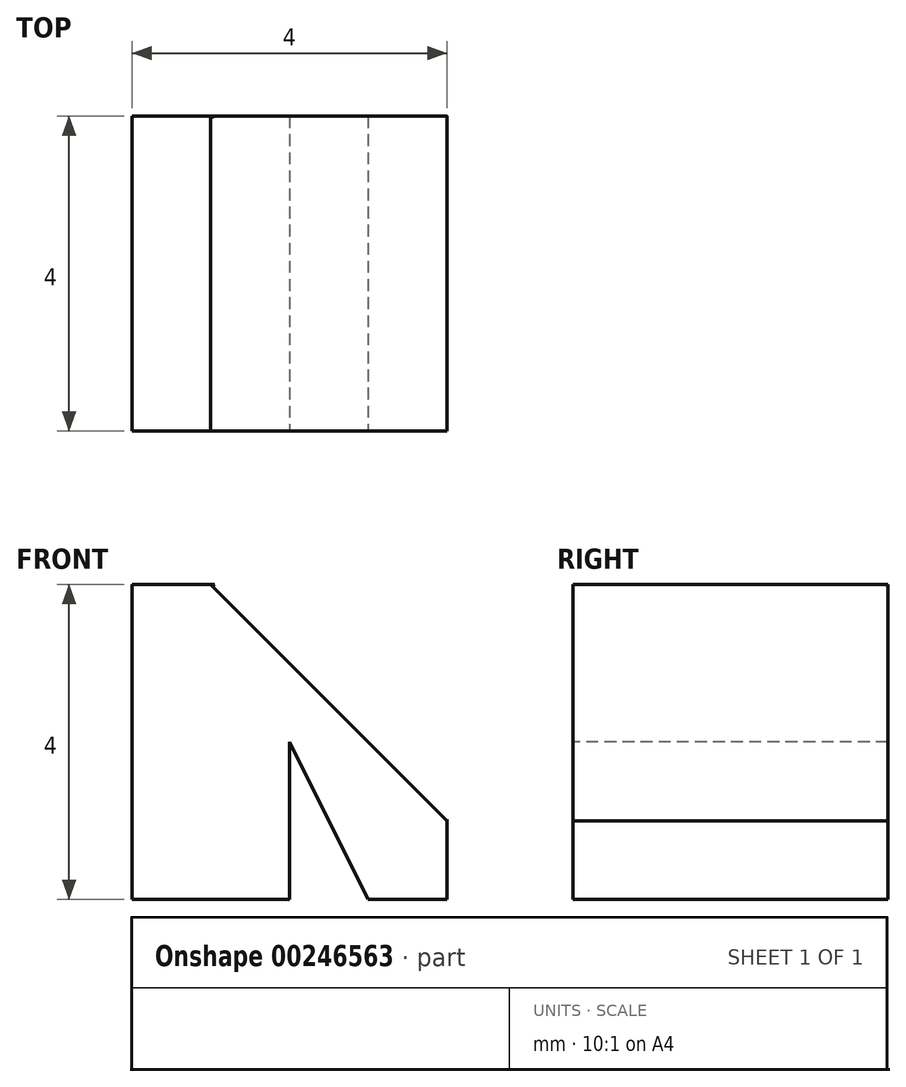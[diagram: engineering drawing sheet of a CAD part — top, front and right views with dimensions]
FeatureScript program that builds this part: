
annotation { "Feature Type Name" : "Feature", "Feature Type Description" : "" }
export const myFeature = defineFeature(function(context is Context, id is Id, definition is map)
    precondition{}
    {
        {
            var Q0;
            Q0=qCreatedBy(makeId("Top.planeOp"),FACE);
            var sketch = newSketch(context, id + "F0", { "sketchPlane" : qUnion([Q0])});
            skLineSegment(sketch, "E0.bottom", {"start": v(0, 0) * mm, "end": v(4, 0) * mm});
            skLineSegment(sketch, "E0.top", {"start": v(0, 4) * mm, "end": v(4, 4) * mm});
            skLineSegment(sketch, "E0.left", {"start": v(0, 0) * mm, "end": v(0, 4) * mm});
            skLineSegment(sketch, "E0.right", {"start": v(4, 0) * mm, "end": v(4, 4) * mm});
            skSolve(sketch);
        }
        {
            var Q0;
            Q0 = qSketchRegion(id + "F0", true);
            extrude(context, id + "F1", {"entities" : qUnion([Q0]), "depth" : 4 * mm});
        }
        {
            var Q0;
            Q0=makeQuery(id+"F1.opExtrude","SWEPT_FACE",FACE,{"disambiguationData":[OSD([sQuery(id+"F0.wireOp",EDGE,"E0.bottom")])]});
            var sketch = newSketch(context, id + "F2", { "sketchPlane" : qUnion([Q0])});
            skLineSegment(sketch, "E1", {"start": v(2, 0) * mm, "end": v(3, 0) * mm});
            skLineSegment(sketch, "E2", {"start": v(2, 0) * mm, "end": v(2, 2) * mm});
            skLineSegment(sketch, "E3", {"start": v(2, 2) * mm, "end": v(3, 0) * mm});
            skSolve(sketch);
        }
        {
            var Q0;
            Q0=makeQuery(id+"F2.imprint","IMPRINT",FACE,{"disambiguationData":[TD([[makeQuery(id+"F2.imprint","IMPRINT",EDGE,{"derivedFrom":sQuery(id+"F2.wireOp",EDGE,"E1")}),1.0]])]});
            extrude(context, id + "F3", {"entities" : qUnion([Q0]), "operationType" : NewBodyOperationType.REMOVE, "oppositeDirection" : true, "depth" : 25 * mm});
        }
        {
            var Q0;
            Q0=makeQuery(id+"F1.opExtrude","SWEPT_FACE",FACE,{"disambiguationData":[OSD([sQuery(id+"F0.wireOp",EDGE,"E0.right")])]});
            var sketch = newSketch(context, id + "F4", { "sketchPlane" : qUnion([Q0])});
            skLineSegment(sketch, "E4", {"start": v(0, 0) * mm, "end": v(0, 1) * mm});
            skLineSegment(sketch, "E5", {"start": v(0, 1) * mm, "end": v(4, 1) * mm});
            skSolve(sketch);
        }
        {
            var Q0;
            Q0=makeQuery(id+"F1.opExtrude","CAP_FACE",FACE,{"disambiguationData":[OSD([sQuery(id+"F0.wireOp",EDGE,"E0.bottom"),sQuery(id+"F0.wireOp",EDGE,"E0.top"),sQuery(id+"F0.wireOp",EDGE,"E0.left"),sQuery(id+"F0.wireOp",EDGE,"E0.right")])],"isStart":false});
            var sketch = newSketch(context, id + "F5", { "sketchPlane" : qUnion([Q0])});
            skLineSegment(sketch, "E6.bottom", {"start": v(0, 0) * mm, "end": v(1, 0) * mm});
            skLineSegment(sketch, "E6.top", {"start": v(0, 4) * mm, "end": v(1, 4) * mm});
            skLineSegment(sketch, "E6.left", {"start": v(0, 0) * mm, "end": v(0, 4) * mm});
            skLineSegment(sketch, "E6.right", {"start": v(1, 0) * mm, "end": v(1, 4) * mm});
            skSolve(sketch);
        }
        {
            var Q0;
            Q0=sQuery(id+"F5.wireOp",VERTEX,"E6.right.start");
            var Q1;
            Q1=sQuery(id+"F4.wireOp",VERTEX,"E5.start");
            var Q2;
            Q2=sQuery(id+"F4.wireOp",VERTEX,"E5.end");
            cPlane(context, id + "F6", {"entities" : qUnion([Q0, Q1, Q2]), "cplaneType" : CPlaneType.THREE_POINT, "offset" : 25 * mm, "width" : 150 * mm, "height" : 150 * mm});
        }
        {
            var Q0;
            Q0=qCreatedBy(id+"F6.planeOp",FACE);
            var sketch = newSketch(context, id + "F7", { "sketchPlane" : qUnion([Q0])});
            skLineSegment(sketch, "E7", {"start": v(0, 2.12) * mm, "end": v(0, -2.12) * mm});
            skLineSegment(sketch, "E8", {"start": v(0, 2.12) * mm, "end": v(-3.98, 2.12) * mm});
            skLineSegment(sketch, "E9", {"start": v(0, -2.12) * mm, "end": v(-4, -2.12) * mm});
            skLineSegment(sketch, "E10", {"start": v(-3.98, 2.12) * mm, "end": v(-4, -2.12) * mm});
            skLineSegment(sketch, "E11", {"start": v(-3.98, 2.12) * mm, "end": v(-5.25, 0.4) * mm});
            skLineSegment(sketch, "E12", {"start": v(-5.25, 0.4) * mm, "end": v(-4, -2.12) * mm});
            skLineSegment(sketch, "E13", {"start": v(0, 2.12) * mm, "end": v(-1.26, 0.4) * mm});
            skLineSegment(sketch, "E14", {"start": v(-1.26, 0.4) * mm, "end": v(-5.25, 0.4) * mm});
            skLineSegment(sketch, "E15", {"start": v(-1.26, 0.4) * mm, "end": v(0, -2.12) * mm});
            skSolve(sketch);
        }
        {
            var Q0;
            Q0 = qSketchRegion(id + "F7", true);
            extrude(context, id + "F8", {"entities" : qUnion([Q0]), "operationType" : NewBodyOperationType.REMOVE, "oppositeDirection" : true, "depth" : 25 * mm});
        }
    });
